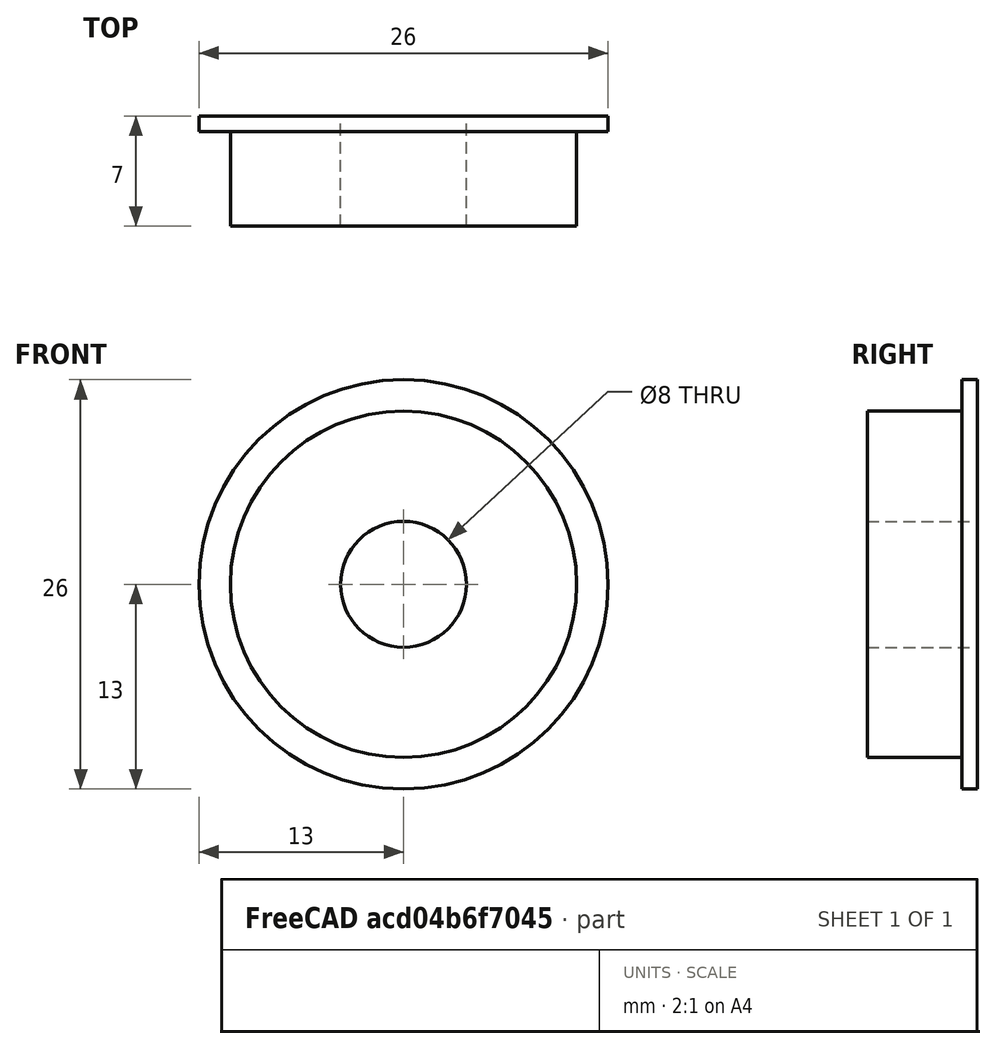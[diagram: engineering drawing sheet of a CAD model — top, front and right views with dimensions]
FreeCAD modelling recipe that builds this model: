
FCSTD DOCUMENT  (FreeCAD 0.15R4669 (Git))
Label: BR_roulementRoue
License: All rights reserved
LicenseURL: http://en.wikipedia.org/wiki/All_rights_reserved
objects: Sketcher::SketchObject×1, Part::Revolution×1
note: 2 computed .brp shape members not serialized (recipe doc carries the construction recipe); baked Part::Feature solids carry a one-line shape summary decoded from their .brp

FEATURE [Sketcher::SketchObject] Sketch  label="coupeRoulement"
  sketch-geometry (6):
    g0: LineSegment StartX=4 StartY=7 StartZ=0 EndX=13 EndY=7 EndZ=0
    g1: LineSegment StartX=13 StartY=7 StartZ=0 EndX=13 EndY=6 EndZ=0
    g2: LineSegment StartX=13 StartY=6 StartZ=0 EndX=11 EndY=6 EndZ=0
    g3: LineSegment StartX=11 StartY=6 StartZ=0 EndX=11 EndY=0 EndZ=0
    g4: LineSegment StartX=11 StartY=0 StartZ=0 EndX=4 EndY=0 EndZ=0
    g5: LineSegment StartX=4 StartY=0 StartZ=0 EndX=4 EndY=7 EndZ=0
  constraints (18):
    c: Horizontal(g0)
    c: Coincident(g0,g1)
    c: Vertical(g1)
    c: Coincident(g1,g2)
    c: Horizontal(g2)
    c: Coincident(g2,g3)
    c: Vertical(g3)
    c: Coincident(g3,g4)
    c: Horizontal(g4)
    c: Coincident(g4,g5)
    c: Coincident(g5,g0)
    c: Vertical(g5)
    c: PointOnObject(g4,g-1)
    c: DistanceX(g-1,g4) = 4
    c: DistanceY(g5) = 7
    c: DistanceX(g-1,g3) = 11
    c: DistanceY(g1) = -1
    c: DistanceX(g-1,g0) = 13
FEATURE [Part::Revolution] Revolve
  Angle = 360
  Axis = (0,1,0)
  Base = (0,0,0)
  Solid = true
  Source = -> Sketch
